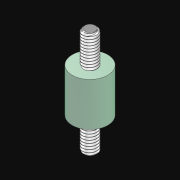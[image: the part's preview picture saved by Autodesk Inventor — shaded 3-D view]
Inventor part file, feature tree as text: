
AUTODESK INVENTOR PART (.ipt)
format: ipt  version: 2021.3 (Build 253353010, 353A)  size: 550,912 bytes
history: native  units: in
note: dims shown in document units (in); Inventor stores cm internally (conversion verified against a paired STEP export)
features: sketch x6, other x3, extrude x2
ambient origin geometry x8: Origin, YZ Plane, XZ Plane, XY Plane, X Axis, Y Axis, Z Axis, Center Point
bodies: Solid1 (feature_tree), Body (feature_tree)
feature tree (11):
  extrude  "Top"  Depth=0.5in TaperAngle=0.0deg
  extrude  "Bottom"  Depth=0.365in TaperAngle=0.0deg
  other  "Top Thread"
  other  "Bottom Thread"
  other  "Taper Ends"
  sketch  "Sketch1"  dims[d0=0.41in d1=0.5in d2=0.0in]
  sketch  "Sketch2"  dims[d3=0.123in d4=0.365in d5=0.0in]
  sketch  "Sketch3"  dims[d6=0.123in]
  sketch  "Sketch4"  dims[d7=0.365in d8=0.0in]
  sketch  "Sketch5"  dims[d9=0.004in]
  sketch  "Sketch6"  dims[d10=60.0deg d11=0.021in d12=0.003in d13=0.031in d14=0.415in d15=0.3937in d16=0.0in d17=90.0deg d18=90.0deg d19=0.0in d20=0.0in d21=60.0deg d22=0.003in d23=0.004in d24=0.021in d25=0.031in d26=0.415in d27=0.3937in d28=0.0in d29=90.0deg d30=90.0deg d31=0.0in d32=0.0in d33=0.059in d34=135.0deg d35=0.0in d36=0.0in d37=90.0deg d38=0.059in d39=135.0deg d40=0.0in]
